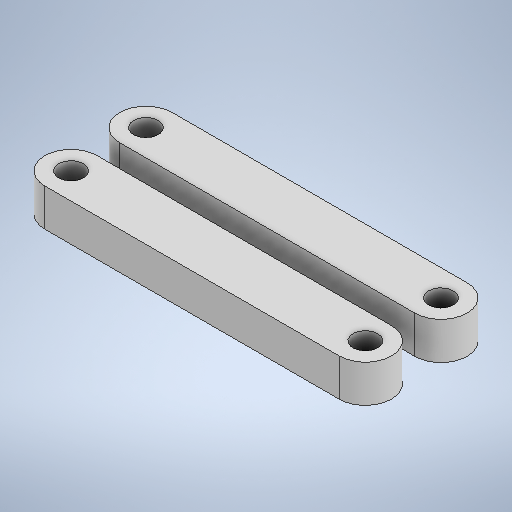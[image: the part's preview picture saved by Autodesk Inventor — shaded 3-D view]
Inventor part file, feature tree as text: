
AUTODESK INVENTOR PART (.ipt)
format: ipt  version: 2025.1 (Build 291241020, 241B)  size: 262,656 bytes
history: native  units: mm
features: move_body x2, sketch x2, other x1, extrude x1, fillet x1, split x1, boolean_combine x1, imported_body x1
ambient origin geometry x8: Origin, YZ Plane, XZ Plane, XY Plane, X Axis, Y Axis, Z Axis, Center Point
bodies: Solid1 (feature_tree), Solid2 (feature_tree), Solid3 (feature_tree), Solid4 (feature_tree)
feature tree (10):
  other  "Repaired Geometry1"
  extrude  "Extrusion1"  Depth=7.0mm
  fillet  "Fillet1"  Radius=3.3mm
  move_body  "Move Body1"
  split  "Split1"
  move_body  "Move Body2"
  boolean_combine  "Combine1"
  sketch  "Sketch1"  dims[d0=7.0mm d1=39.4mm d2=3.3mm]
  imported_body  "Base1"
  sketch  "Sketch2"  dims[d3=3.3mm d4=3.5mm d5=3.5mm d6=5.0mm d7=0.0mm d8=3.5mm d9=0.0mm d10=0.0mm d11=10.0mm d12=-0.1mm d13=0.0mm d14=0.0mm]
